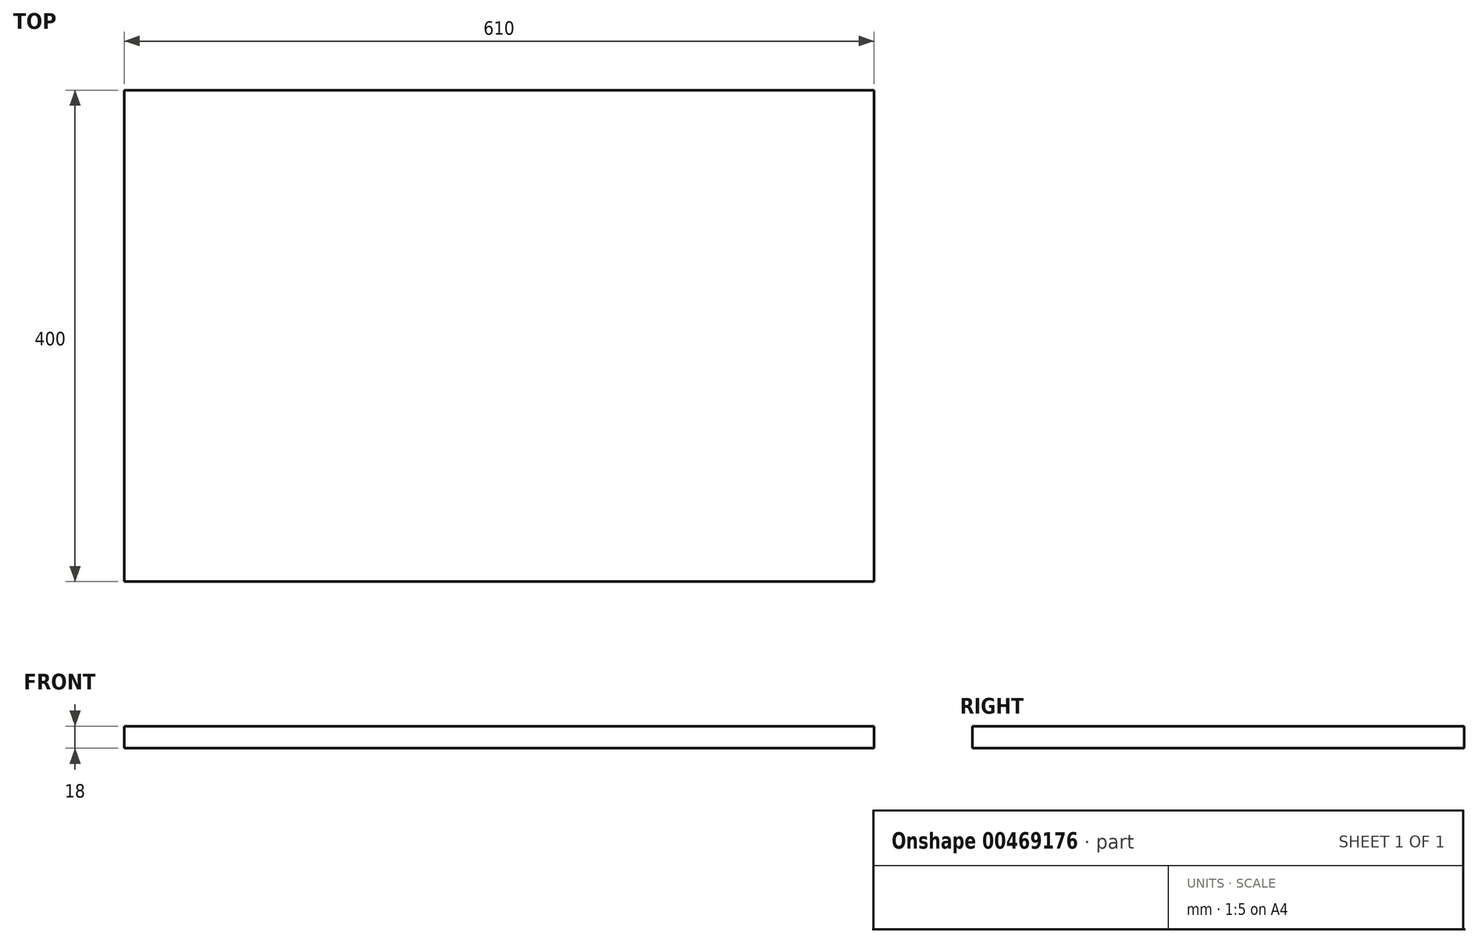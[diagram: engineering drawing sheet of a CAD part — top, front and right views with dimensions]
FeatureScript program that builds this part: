
annotation { "Feature Type Name" : "Feature", "Feature Type Description" : "" }
export const myFeature = defineFeature(function(context is Context, id is Id, definition is map)
    precondition{}
    {
        {
            var Q0;
            Q0=qCreatedBy(makeId("Top.planeOp"),FACE);
            var sketch = newSketch(context, id + "F0", { "sketchPlane" : qUnion([Q0])});
            skLineSegment(sketch, "E0.bottom", {"start": v(0, 400) * mm, "end": v(610, 400) * mm});
            skLineSegment(sketch, "E0.top", {"start": v(0, 0) * mm, "end": v(610, 0) * mm});
            skLineSegment(sketch, "E0.left", {"start": v(0, 400) * mm, "end": v(0, 0) * mm});
            skLineSegment(sketch, "E0.right", {"start": v(610, 400) * mm, "end": v(610, 0) * mm});
            skSolve(sketch);
        }
        {
            var Q0;
            Q0=makeQuery(id+"F0.imprint","IMPRINT",FACE,{"disambiguationData":[TD([[makeQuery(id+"F0.imprint","IMPRINT",EDGE,{"derivedFrom":sQuery(id+"F0.wireOp",EDGE,"E0.bottom")}),-1.0]])]});
            extrude(context, id + "F1", {"entities" : qUnion([Q0]), "depth" : 18 * mm});
        }
    });
